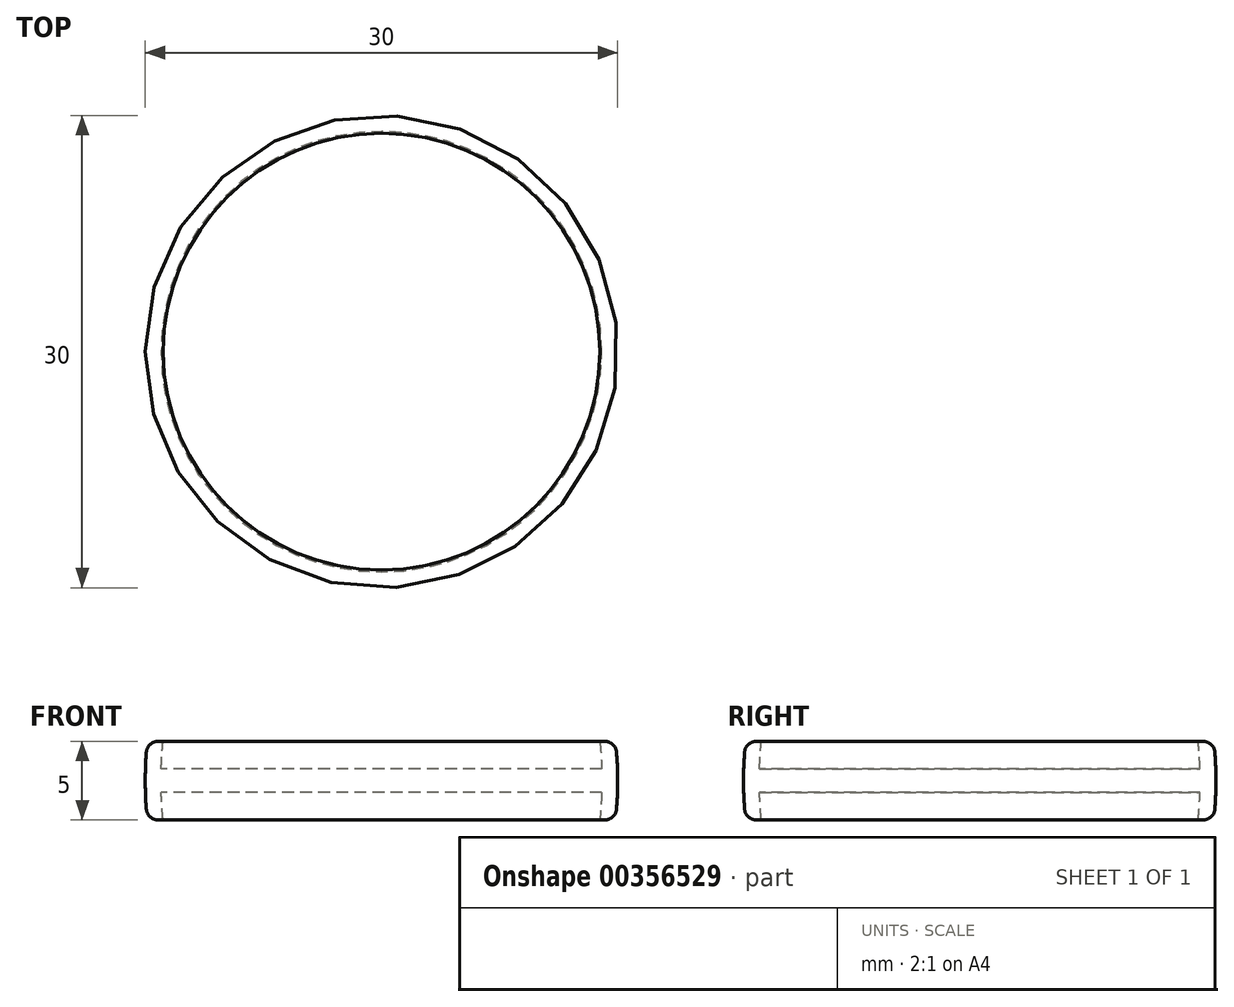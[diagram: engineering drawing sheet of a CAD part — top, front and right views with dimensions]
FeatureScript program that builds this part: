
annotation { "Feature Type Name" : "Feature", "Feature Type Description" : "" }
export const myFeature = defineFeature(function(context is Context, id is Id, definition is map)
    precondition{}
    {
        {
            var Q0;
            Q0=qCreatedBy(makeId("Front.planeOp"),FACE);
            var sketch = newSketch(context, id + "F0", { "sketchPlane" : qUnion([Q0])});
            skLineSegment(sketch, "E0", {"start": v(0, 0) * mm, "end": v(0, -0.75) * mm});
            skLineSegment(sketch, "E1", {"start": v(0, -0.75) * mm, "end": v(-13.99, -0.75) * mm});
            skCircle(sketch, "E2", {"center": v(10, 0) * mm, "radius": 25 * mm});
            skCircle(sketch, "E3", {"center": v(10, 0) * mm, "radius": 24 * mm});
            skLineSegment(sketch, "E4", {"start": v(-13.87, -2.5) * mm, "end": v(-14.87, -2.5) * mm});
            skLineSegment(sketch, "E5.MirrorCS", {"start": v(-13.87, 2.5) * mm, "end": v(-14.87, 2.5) * mm});
            skLineSegment(sketch, "E6.MirrorCS", {"start": v(0, 0.75) * mm, "end": v(-13.99, 0.75) * mm});
            skLineSegment(sketch, "E7.MirrorCS", {"start": v(0, 0) * mm, "end": v(0, 0.75) * mm});
            skSolve(sketch);
        }
        {
            var Q0;
            {var subQ2=sQuery(id+"F0.wireOp",EDGE,"E4");Q0=makeQuery(id+"F0.imprint","IMPRINT",FACE,{"disambiguationData":[TD([[makeQuery(id+"F0.imprint","IMPRINT",EDGE,{"derivedFrom":subQ2}),-1.0]])]});}
            var Q1;
            Q1=makeQuery(id+"F0.imprint","IMPRINT",FACE,{"disambiguationData":[TD([[makeQuery(id+"F0.imprint","IMPRINT",EDGE,{"derivedFrom":sQuery(id+"F0.wireOp",EDGE,"E0")}),-1.0]])]});
            var Q2;
            Q2=sQuery(id+"F0.wireOp",EDGE,"E0");
            revolve(context, id + "F1", {"entities" : qUnion([Q0, Q1]), "axis" : qUnion([Q2]), "revolveType" : RevolveType.FULL});
        }
        {
            var Q0;
            Q0=makeQuery(id+"F1.opRevolve","SWEPT_EDGE",EDGE,{"disambiguationData":[OSD([sQuery(id+"F0.wireOp",EDGE,"E2"),sQuery(id+"F0.wireOp",EDGE,"E5.MirrorCS")])]});
            var Q1;
            Q1=makeQuery(id+"F1.opRevolve","SWEPT_EDGE",EDGE,{"disambiguationData":[OSD([sQuery(id+"F0.wireOp",EDGE,"E2"),sQuery(id+"F0.wireOp",EDGE,"E4")])]});
            fillet(context, id + "F2", {"entities" : qUnion([Q0, Q1]), "radius" : 0.75 * mm, "tangentPropagation" : true, "allowEdgeOverflow" : false});
        }
    });
